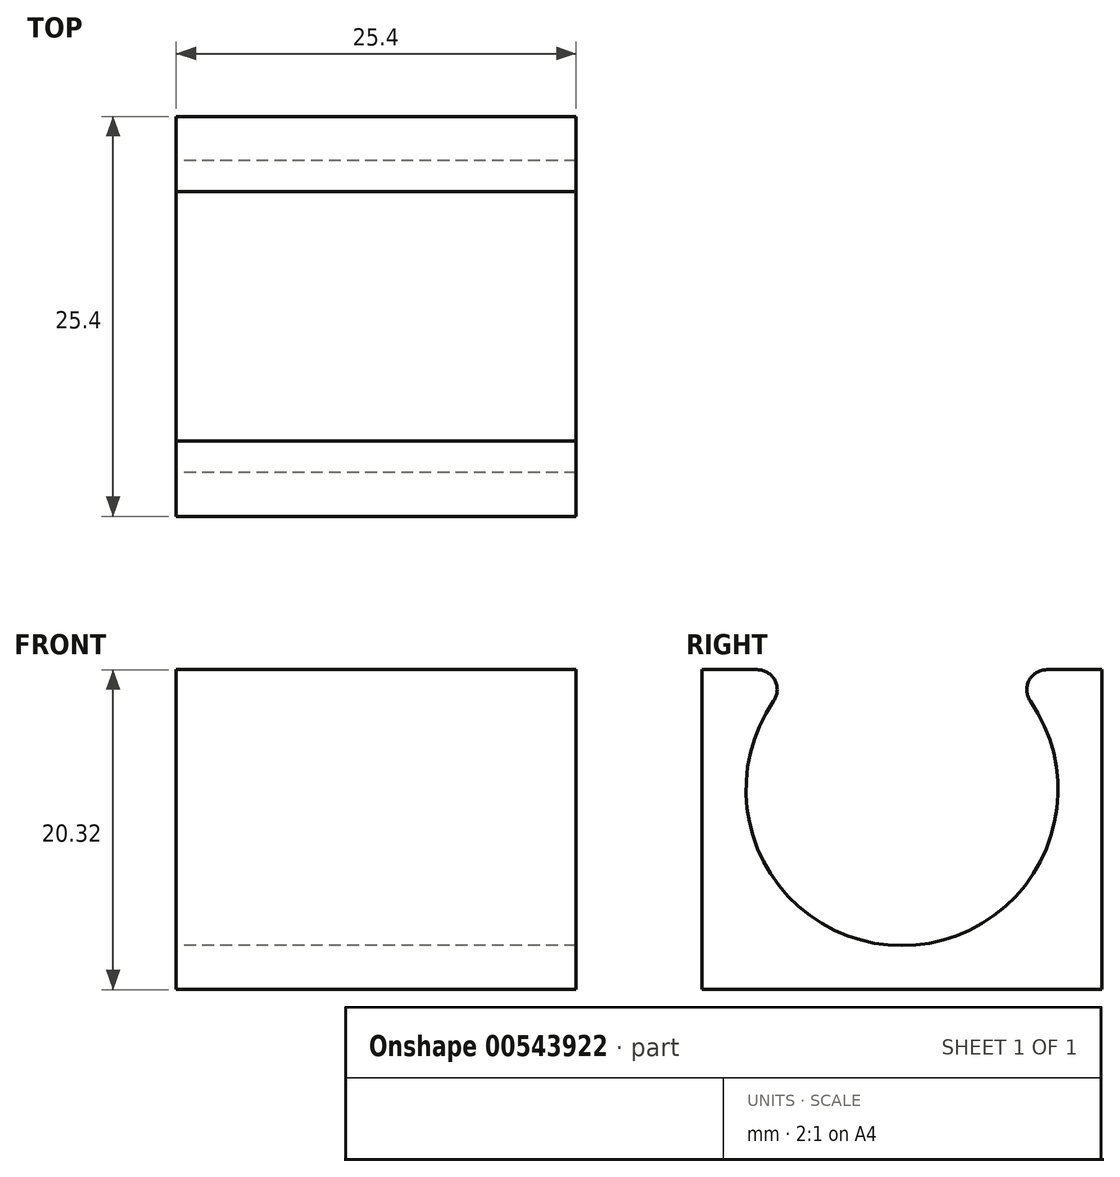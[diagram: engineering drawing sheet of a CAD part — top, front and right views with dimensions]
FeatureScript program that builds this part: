
annotation { "Feature Type Name" : "Feature", "Feature Type Description" : "" }
export const myFeature = defineFeature(function(context is Context, id is Id, definition is map)
    precondition{}
    {
        {
            var Q0;
            Q0=qCreatedBy(makeId("Right.planeOp"),FACE);
            var sketch = newSketch(context, id + "F0", { "sketchPlane" : qUnion([Q0])});
            skLineSegment(sketch, "E0", {"start": v(13.15, 11.13) * mm, "end": v(38.55, 11.13) * mm});
            skLineSegment(sketch, "E1", {"start": v(38.55, 11.13) * mm, "end": v(38.55, 31.45) * mm});
            skLineSegment(sketch, "E2", {"start": v(38.55, 31.45) * mm, "end": v(32.18, 31.45) * mm});
            skArc(sketch, "E3", {"start": v(19.52, 31.45) * mm, "mid": v(25.85, 13.93) * mm, "end": v(32.18, 31.45) * mm});
            skLineSegment(sketch, "E4.trimOffspring", {"start": v(19.52, 31.45) * mm, "end": v(13.15, 31.45) * mm});
            skLineSegment(sketch, "E5", {"start": v(13.15, 31.45) * mm, "end": v(13.15, 11.13) * mm});
            skSolve(sketch);
        }
        {
            var Q0;
            Q0 = qSketchRegion(id + "F0", true);
            extrude(context, id + "F1", {"entities" : qUnion([Q0]), "depth" : 25.4 * mm, "offsetDistance" : 25.4 * mm});
        }
        {
            var Q0;
            Q0=makeQuery(id+"F1.opExtrude","SWEPT_EDGE",EDGE,{"disambiguationData":[OSD([sQuery(id+"F0.wireOp",EDGE,"E2"),sQuery(id+"F0.wireOp",EDGE,"E3")])]});
            var Q1;
            Q1=makeQuery(id+"F1.opExtrude","SWEPT_EDGE",EDGE,{"disambiguationData":[OSD([sQuery(id+"F0.wireOp",EDGE,"E3"),sQuery(id+"F0.wireOp",EDGE,"E4.trimOffspring")])]});
            fillet(context, id + "F2", {"entities" : qUnion([Q0, Q1]), "radius" : 1.27 * mm, "tangentPropagation" : true, "allowEdgeOverflow" : false});
        }
    });
